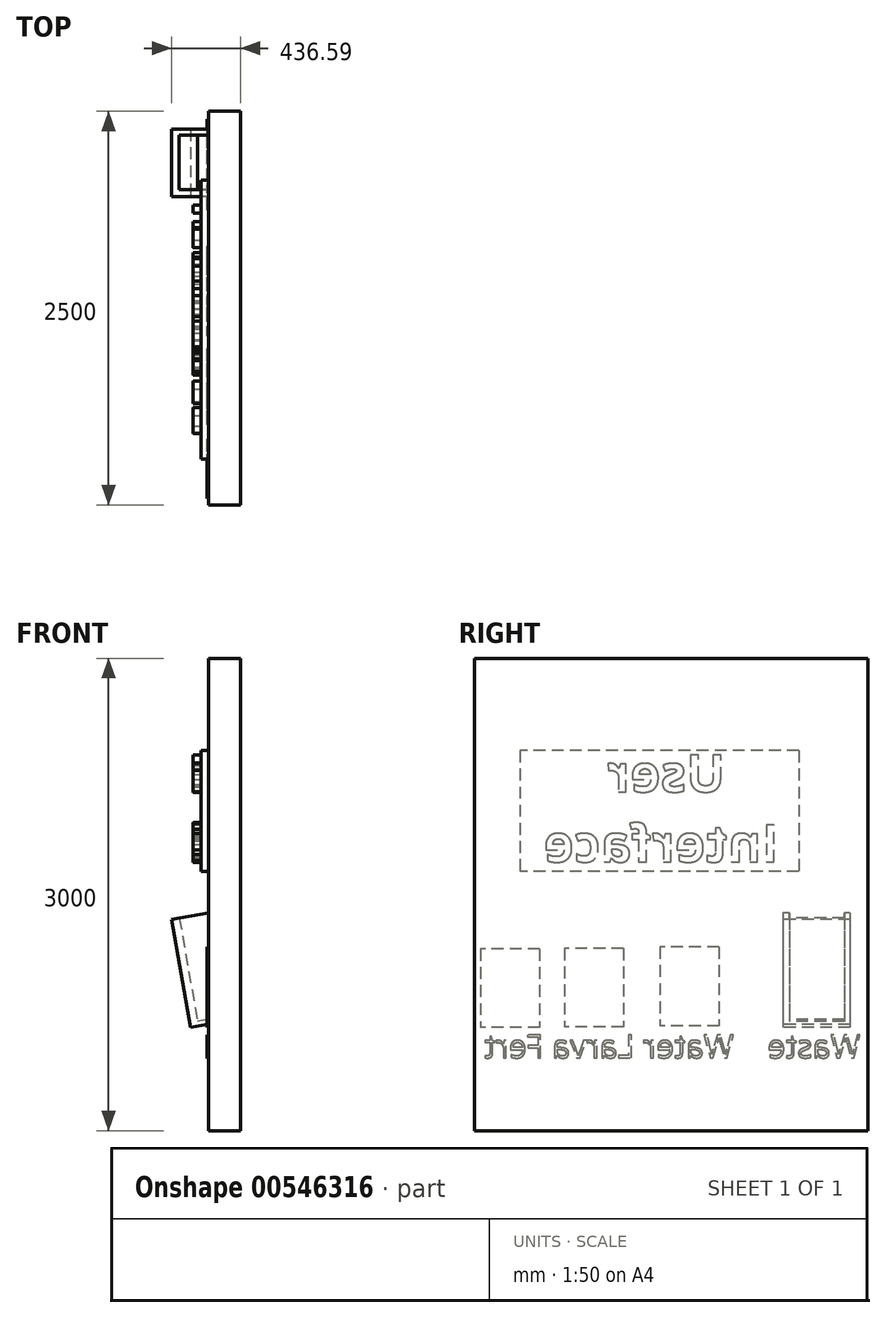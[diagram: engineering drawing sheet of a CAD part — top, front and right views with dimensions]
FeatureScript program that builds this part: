
annotation { "Feature Type Name" : "Feature", "Feature Type Description" : "" }
export const myFeature = defineFeature(function(context is Context, id is Id, definition is map)
    precondition{}
    {
        {
            var Q0;
            Q0=qCreatedBy(makeId("Right.planeOp"),FACE);
            var sketch = newSketch(context, id + "F0", { "sketchPlane" : qUnion([Q0])});
            skLineSegment(sketch, "E0.bottom", {"start": v(0, 0) * mm, "end": v(2500, 0) * mm});
            skLineSegment(sketch, "E0.top", {"start": v(0, 3000) * mm, "end": v(2500, 3000) * mm});
            skLineSegment(sketch, "E0.left", {"start": v(0, 0) * mm, "end": v(0, 3000) * mm});
            skLineSegment(sketch, "E0.right", {"start": v(2500, 0) * mm, "end": v(2500, 3000) * mm});
            skSolve(sketch);
        }
        {
            var Q0;
            Q0=qSketchRegion(id+"F0",true);
            extrude(context, id + "F1", {"entities" : qUnion([Q0]), "oppositeDirection" : true, "depth" : 200 * mm});
        }
        {
            var Q0;
            Q0=makeQuery(id+"F1.opExtrude","CAP_FACE",FACE,{"disambiguationData":[OSD([sQuery(id+"F0.wireOp",EDGE,"E0.bottom"),sQuery(id+"F0.wireOp",EDGE,"E0.top"),sQuery(id+"F0.wireOp",EDGE,"E0.left"),sQuery(id+"F0.wireOp",EDGE,"E0.right")])],"isStart":false});
            var Q1;
            Q1=makeQuery(id+"F1.opExtrude","CAP_EDGE",EDGE,{"disambiguationData":[OSD([sQuery(id+"F0.wireOp",EDGE,"E0.bottom")])],"isStart":false});
            cPlane(context, id + "F2", {"entities" : qUnion([Q0, Q1]), "cplaneType" : CPlaneType.LINE_ANGLE, "offset" : 25 * mm, "angle" : 10 * degree, "oppositeDirection" : true, "width" : 150 * mm, "height" : 150 * mm});
        }
        {
            var Q0;
            Q0=qCreatedBy(id+"F2.planeOp",FACE);
            var sketch = newSketch(context, id + "F3", { "sketchPlane" : qUnion([Q0])});
            skLineSegment(sketch, "E1.bottom", {"start": v(2386.12, 1397.22) * mm, "end": v(1959.2, 1397.22) * mm});
            skLineSegment(sketch, "E1.top", {"start": v(2386.12, 700.52) * mm, "end": v(1959.2, 700.52) * mm});
            skLineSegment(sketch, "E1.left", {"start": v(2386.12, 1397.22) * mm, "end": v(2386.12, 700.52) * mm});
            skLineSegment(sketch, "E1.right", {"start": v(1959.2, 1397.22) * mm, "end": v(1959.2, 700.52) * mm});
            skSolve(sketch);
        }
        {
            var Q0;
            Q0=qSketchRegion(id+"F3",true);
            extrude(context, id + "F4", {"entities" : qUnion([Q0]), "operationType" : NewBodyOperationType.ADD, "endBound" : BoundingType.UP_TO_NEXT, "depth" : 25 * mm});
        }
        {
            var Q0;
            Q0=qCreatedBy(id+"F2.planeOp",FACE);
            cPlane(context, id + "F5", {"entities" : qUnion([Q0]), "cplaneType" : CPlaneType.OFFSET, "offset" : 50 * mm, "width" : 150 * mm, "height" : 150 * mm});
        }
        {
            var Q0;
            Q0=qCreatedBy(id+"F5.planeOp",FACE);
            var sketch = newSketch(context, id + "F6", { "sketchPlane" : qUnion([Q0])});
            skLineSegment(sketch, "E2.bottom", {"start": v(2349.67, 1482.87) * mm, "end": v(2000.93, 1482.87) * mm});
            skLineSegment(sketch, "E2.top", {"start": v(2349.67, 730.76) * mm, "end": v(2000.93, 730.76) * mm});
            skLineSegment(sketch, "E2.left", {"start": v(2349.67, 1482.87) * mm, "end": v(2349.67, 730.76) * mm});
            skLineSegment(sketch, "E2.right", {"start": v(2000.93, 1482.87) * mm, "end": v(2000.93, 730.76) * mm});
            skSolve(sketch);
        }
        {
            var Q0;
            Q0=qSketchRegion(id+"F6",true);
            var Q1;
            Q1=makeQuery(id+"F1.opExtrude","CAP_FACE",FACE,{"disambiguationData":[OSD([sQuery(id+"F0.wireOp",EDGE,"E0.bottom"),sQuery(id+"F0.wireOp",EDGE,"E0.top"),sQuery(id+"F0.wireOp",EDGE,"E0.left"),sQuery(id+"F0.wireOp",EDGE,"E0.right")])],"isStart":false});
            extrude(context, id + "F7", {"entities" : qUnion([Q0]), "operationType" : NewBodyOperationType.REMOVE, "endBound" : BoundingType.UP_TO_SURFACE, "endBoundEntityFace" : qUnion([Q1]), "depth" : 25 * mm});
        }
        {
            var Q0;
            {var subQ0=sQuery(id+"F0.wireOp",EDGE,"E0.right");var subQ1=sQuery(id+"F0.wireOp",EDGE,"E0.left");var subQ2=sQuery(id+"F0.wireOp",EDGE,"E0.top");var subQ3=sQuery(id+"F0.wireOp",EDGE,"E0.bottom");Q0=makeQuery(id+"F7.boolean.opBoolean","MERGE",FACE,{"derivedFrom":[makeQuery(id+"F1.opExtrude","CAP_FACE",FACE,{"disambiguationData":[OSD([subQ3,subQ2,subQ1,subQ0])],"isStart":false}),makeQuery(id+"F7.opExtrude","CAP_FACE",FACE,{"disambiguationData":[OSD([subQ3,subQ2,subQ1,subQ0])],"isStart":false})]});}
            var sketch = newSketch(context, id + "F8", { "sketchPlane" : qUnion([Q0])});
            skLineSegment(sketch, "E3.bottom", {"start": v(-2061.31, 2414.44) * mm, "end": v(-290.44, 2414.44) * mm});
            skLineSegment(sketch, "E3.top", {"start": v(-2061.31, 1646.86) * mm, "end": v(-290.44, 1646.86) * mm});
            skLineSegment(sketch, "E3.left", {"start": v(-2061.31, 2414.44) * mm, "end": v(-2061.31, 1646.86) * mm});
            skLineSegment(sketch, "E3.right", {"start": v(-290.44, 2414.44) * mm, "end": v(-290.44, 1646.86) * mm});
            skSolve(sketch);
        }
        {
            var Q0;
            Q0=qSketchRegion(id+"F8",true);
            extrude(context, id + "F9", {"entities" : qUnion([Q0]), "operationType" : NewBodyOperationType.ADD, "depth" : 50 * mm});
        }
        {
            var Q0;
            Q0=makeQuery(id+"F9.opExtrude","CAP_FACE",FACE,{"disambiguationData":[OSD([sQuery(id+"F8.wireOp",EDGE,"E3.bottom"),sQuery(id+"F8.wireOp",EDGE,"E3.top"),sQuery(id+"F8.wireOp",EDGE,"E3.left"),sQuery(id+"F8.wireOp",EDGE,"E3.right")])],"isStart":false});
            var sketch = newSketch(context, id + "F10", { "sketchPlane" : qUnion([Q0])});
            skText(sketch, "E4", { "text": "    User \nInterface", "fontName": "OpenSans-Bold.ttf"});
            const initialGuessF10  = {"E4": [-1.93223, 2.1521, 1, 0, 0.23553]};
            skSetInitialGuess(sketch, initialGuessF10);
            skSolve(sketch);
        }
        {
            var Q0;
            Q0=qSketchRegion(id+"F10",true);
            var Q1;
            Q1=qConstructionFilter(qBodyType(qCreatedBy(id+"F10",EDGE),BodyType.WIRE),ConstructionObject.NO);
            extrude(context, id + "F11", {"entities" : qUnion([Q0]), "operationType" : NewBodyOperationType.ADD, "surfaceEntities" : qUnion([Q1]), "depth" : 50 * mm});
        }
        {
            var Q0;
            {var subQ0=sQuery(id+"F0.wireOp",EDGE,"E0.right");var subQ1=sQuery(id+"F0.wireOp",EDGE,"E0.left");var subQ2=sQuery(id+"F0.wireOp",EDGE,"E0.top");var subQ3=sQuery(id+"F0.wireOp",EDGE,"E0.bottom");Q0=makeQuery(id+"F7.boolean.opBoolean","MERGE",FACE,{"derivedFrom":[makeQuery(id+"F1.opExtrude","CAP_FACE",FACE,{"disambiguationData":[OSD([subQ3,subQ2,subQ1,subQ0])],"isStart":false}),makeQuery(id+"F7.opExtrude","CAP_FACE",FACE,{"disambiguationData":[OSD([subQ3,subQ2,subQ1,subQ0])],"isStart":false})]});}
            var sketch = newSketch(context, id + "F12", { "sketchPlane" : qUnion([Q0])});
            skLineSegment(sketch, "E5.bottom", {"start": v(-1553.95, 1166.36) * mm, "end": v(-1178.95, 1166.36) * mm});
            skLineSegment(sketch, "E5.top", {"start": v(-1553.95, 666.36) * mm, "end": v(-1178.95, 666.36) * mm});
            skLineSegment(sketch, "E5.left", {"start": v(-1553.95, 1166.36) * mm, "end": v(-1553.95, 666.36) * mm});
            skLineSegment(sketch, "E5.right", {"start": v(-1178.95, 1166.36) * mm, "end": v(-1178.95, 666.36) * mm});
            skText(sketch, "E6", { "text": "Waste    Water Larva Fert", "fontName": "OpenSans-Regular.ttf"});
            skLineSegment(sketch, "E7.bottom", {"start": v(-945.93, 1158) * mm, "end": v(-570.93, 1158) * mm});
            skLineSegment(sketch, "E7.top", {"start": v(-945.93, 658) * mm, "end": v(-570.93, 658) * mm});
            skLineSegment(sketch, "E7.left", {"start": v(-945.93, 1158) * mm, "end": v(-945.93, 658) * mm});
            skLineSegment(sketch, "E7.right", {"start": v(-570.93, 1158) * mm, "end": v(-570.93, 658) * mm});
            skLineSegment(sketch, "E8.bottom", {"start": v(-414.75, 1154.44) * mm, "end": v(-39.75, 1154.44) * mm});
            skLineSegment(sketch, "E8.top", {"start": v(-414.75, 654.44) * mm, "end": v(-39.75, 654.44) * mm});
            skLineSegment(sketch, "E8.left", {"start": v(-414.75, 1154.44) * mm, "end": v(-414.75, 654.44) * mm});
            skLineSegment(sketch, "E8.right", {"start": v(-39.75, 1154.44) * mm, "end": v(-39.75, 654.44) * mm});
            const initialGuessF12  = {"E6": [-2.45216, 0.46246, 1, 0, 0.14821]};
            skSetInitialGuess(sketch, initialGuessF12);
            skSolve(sketch);
        }
        {
            var Q0;
            Q0=qSketchRegion(id+"F12",true);
            extrude(context, id + "F13", {"entities" : qUnion([Q0]), "operationType" : NewBodyOperationType.ADD, "depth" : 10 * mm});
        }
    });
